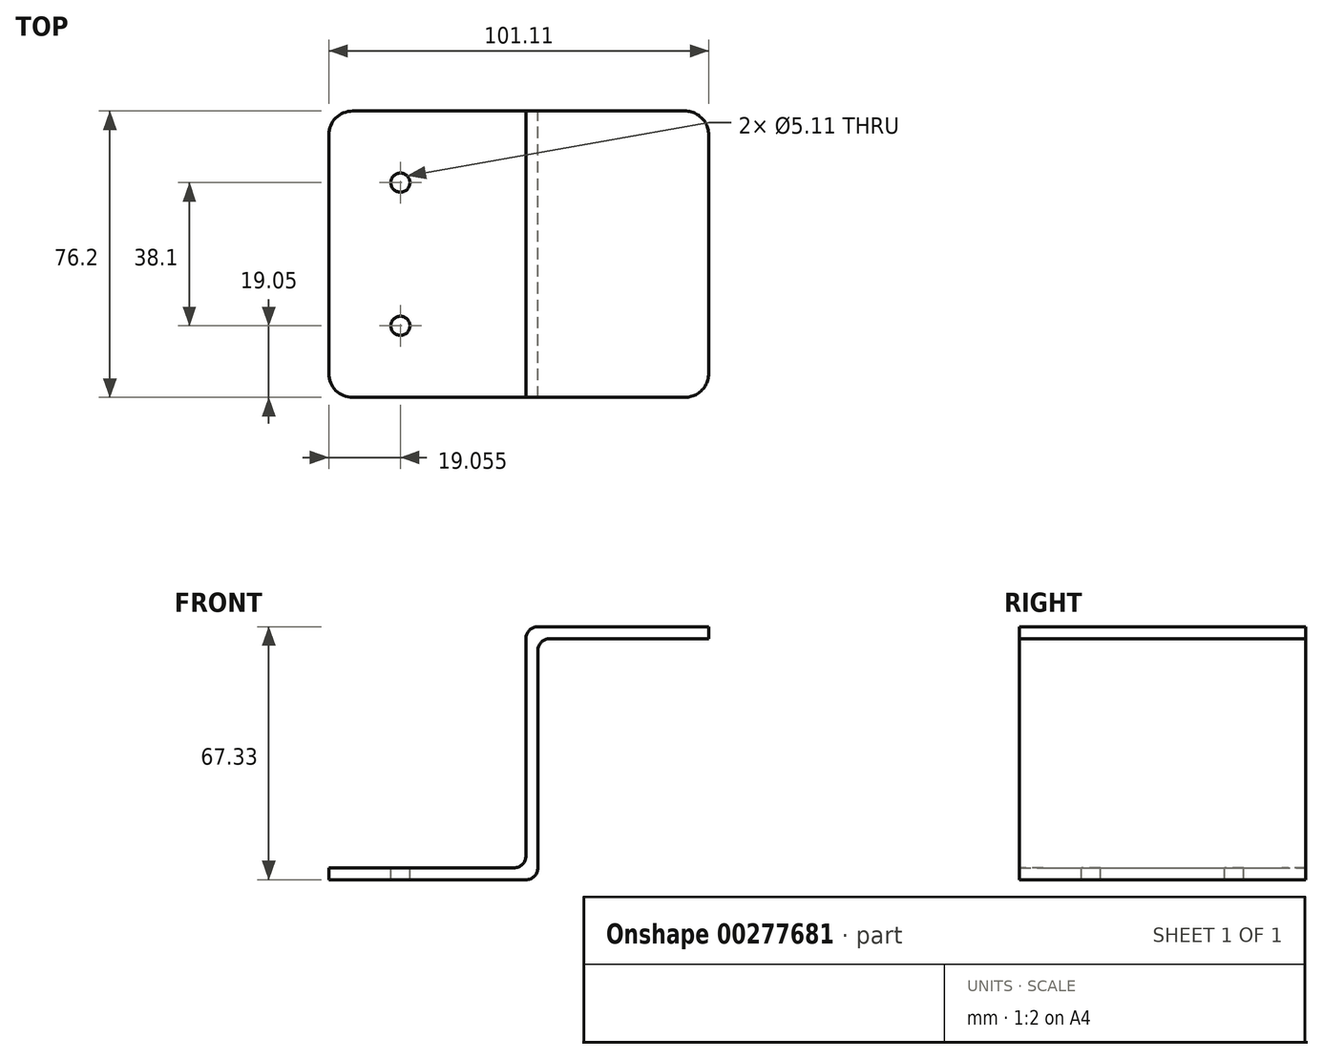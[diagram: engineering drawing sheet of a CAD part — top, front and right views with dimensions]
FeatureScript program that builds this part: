
annotation { "Feature Type Name" : "Feature", "Feature Type Description" : "" }
export const myFeature = defineFeature(function(context is Context, id is Id, definition is map)
    precondition{}
    {
        {
            var Q0;
            Q0=qCreatedBy(makeId("Front.planeOp"),FACE);
            var sketch = newSketch(context, id + "F0", { "sketchPlane" : qUnion([Q0])});
            skLineSegment(sketch, "E0.bottom", {"start": v(-27.82, -1.59) * mm, "end": v(27.82, -1.59) * mm});
            skLineSegment(sketch, "E0.top", {"start": v(-27.82, 1.59) * mm, "end": v(24.64, 1.59) * mm});
            skLineSegment(sketch, "E0.left", {"start": v(-27.82, -1.59) * mm, "end": v(-27.82, 1.59) * mm});
            skLineSegment(sketch, "E0.right", {"start": v(27.82, -1.59) * mm, "end": v(27.82, 1.59) * mm});
            skPoint(sketch, "E0.middle", {"position": v(0, 0) * mm});
            skLineSegment(sketch, "E1.bottom", {"start": v(27.82, 62.56) * mm, "end": v(73.29, 62.56) * mm});
            skLineSegment(sketch, "E1.top", {"start": v(27.82, 65.74) * mm, "end": v(73.29, 65.74) * mm});
            skLineSegment(sketch, "E1.right", {"start": v(73.29, 62.56) * mm, "end": v(73.29, 65.74) * mm});
            skPoint(sketch, "E1.middle", {"position": v(50.55, 64.15) * mm});
            skLineSegment(sketch, "E2", {"start": v(27.82, 1.59) * mm, "end": v(27.82, 62.56) * mm});
            skLineSegment(sketch, "E3.0", {"start": v(24.64, 9.6) * mm, "end": v(24.64, 62.56) * mm});
            skLineSegment(sketch, "E4", {"start": v(24.64, 62.56) * mm, "end": v(24.64, 65.74) * mm});
            skLineSegment(sketch, "E5", {"start": v(27.82, 65.74) * mm, "end": v(24.64, 65.74) * mm});
            skLineSegment(sketch, "E6", {"start": v(24.64, 9.6) * mm, "end": v(24.64, 1.59) * mm});
            skSolve(sketch);
        }
        {
            var Q0;
            Q0 = qSketchRegion(id + "F0", true);
            extrude(context, id + "F1", {"entities" : qUnion([Q0]), "endBound" : BoundingType.SYMMETRIC, "depth" : 76.2 * mm});
        }
        {
            var Q0;
            Q0=makeQuery(id+"F1.opExtrude","CAP_EDGE",EDGE,{"disambiguationData":[OSD([sQuery(id+"F0.wireOp",EDGE,"E0.left")])],"isStart":false});
            fillet(context, id + "F2", {"entities" : qUnion([Q0]), "radius" : 6.35 * mm, "tangentPropagation" : true, "allowEdgeOverflow" : false});
        }
        {
            var Q0;
            Q0=makeQuery(id+"F1.opExtrude","CAP_EDGE",EDGE,{"disambiguationData":[OSD([sQuery(id+"F0.wireOp",EDGE,"E1.right")])],"isStart":true});
            var Q1;
            Q1=makeQuery(id+"F1.opExtrude","CAP_EDGE",EDGE,{"disambiguationData":[OSD([sQuery(id+"F0.wireOp",EDGE,"E1.right")])],"isStart":false});
            var Q2;
            Q2=makeQuery(id+"F1.opExtrude","CAP_EDGE",EDGE,{"disambiguationData":[OSD([sQuery(id+"F0.wireOp",EDGE,"E0.left")])],"isStart":true});
            fillet(context, id + "F3", {"entities" : qUnion([Q0, Q1, Q2]), "radius" : 6.35 * mm, "tangentPropagation" : true, "allowEdgeOverflow" : false});
        }
        {
            var Q0;
            Q0=makeQuery(id+"F1.opExtrude","SWEPT_FACE",FACE,{"disambiguationData":[OSD([sQuery(id+"F0.wireOp",EDGE,"E0.top")])]});
            var sketch = newSketch(context, id + "F4", { "sketchPlane" : qUnion([Q0])});
            skLineSegment(sketch, "E7", {"start": v(-8.77, 0) * mm, "end": v(-8.77, -19.05) * mm});
            skLineSegment(sketch, "E8", {"start": v(-8.77, 0) * mm, "end": v(-8.77, 19.05) * mm});
            skSolve(sketch);
        }
        {
            var Q0;
            Q0=sQuery(id+"F4.wireOp",VERTEX,"E8.end");
            var Q1;
            Q1=sQuery(id+"F4.wireOp",VERTEX,"E7.end");
            var Q2;
            Q2=makeQuery(id+"F1.opExtrude","SWEPT_BODY",BODY,{"disambiguationData":[OSD([sQuery(id+"F0.wireOp",EDGE,"E0.bottom"),sQuery(id+"F0.wireOp",EDGE,"E0.top"),sQuery(id+"F0.wireOp",EDGE,"E0.left"),sQuery(id+"F0.wireOp",EDGE,"E0.right"),sQuery(id+"F0.wireOp",EDGE,"E1.bottom"),sQuery(id+"F0.wireOp",EDGE,"E1.top"),sQuery(id+"F0.wireOp",EDGE,"E1.right"),sQuery(id+"F0.wireOp",EDGE,"E2"),sQuery(id+"F0.wireOp",EDGE,"E3.0"),sQuery(id+"F0.wireOp",EDGE,"E4"),sQuery(id+"F0.wireOp",EDGE,"E5"),sQuery(id+"F0.wireOp",EDGE,"E6")])]});
            hole(context, id + "F5", {"style" : HoleStyle.SIMPLE, "endStyle" : HoleEndStyle.THROUGH, "standardTappedOrClearance" : lookupTablePath({ "standard" : "ANSI", "fit" : "Normal (ASME)", "size" : "#10", "type" : "Clearance" }), "standardBlindInLast" : lookupTablePath({ "fit" : "Free", "standard" : "ANSI", "size" : "#10", "type" : "Clearance" }), "holeDiameter" : 5.1 * mm, "tappedDepth" : 12.7 * mm, "tapClearance" : 3, "startFromSketch" : true, "locations" : qUnion([Q0, Q1]), "scope" : qUnion([Q2])});
        }
        {
            var Q0;
            Q0=makeQuery(id+"F1.opExtrude","SWEPT_EDGE",EDGE,{"disambiguationData":[OSD([sQuery(id+"F0.wireOp",EDGE,"E4"),sQuery(id+"F0.wireOp",EDGE,"E5")])]});
            var Q1;
            Q1=makeQuery(id+"F1.opExtrude","SWEPT_EDGE",EDGE,{"disambiguationData":[OSD([sQuery(id+"F0.wireOp",EDGE,"E0.bottom"),sQuery(id+"F0.wireOp",EDGE,"E0.right")])]});
            fillet(context, id + "F6", {"entities" : qUnion([Q0, Q1]), "radius" : 3.17 * mm, "tangentPropagation" : true, "allowEdgeOverflow" : false});
        }
        {
            var Q0;
            Q0=makeQuery(id+"F1.opExtrude","SWEPT_EDGE",EDGE,{"disambiguationData":[OSD([sQuery(id+"F0.wireOp",EDGE,"E1.bottom"),sQuery(id+"F0.wireOp",EDGE,"E2")])]});
            var Q1;
            Q1=makeQuery(id+"F1.opExtrude","SWEPT_EDGE",EDGE,{"disambiguationData":[OSD([sQuery(id+"F0.wireOp",EDGE,"E0.top"),sQuery(id+"F0.wireOp",EDGE,"E6")])]});
            fillet(context, id + "F7", {"entities" : qUnion([Q0, Q1]), "radius" : 3.17 * mm, "tangentPropagation" : true, "allowEdgeOverflow" : false});
        }
    });
